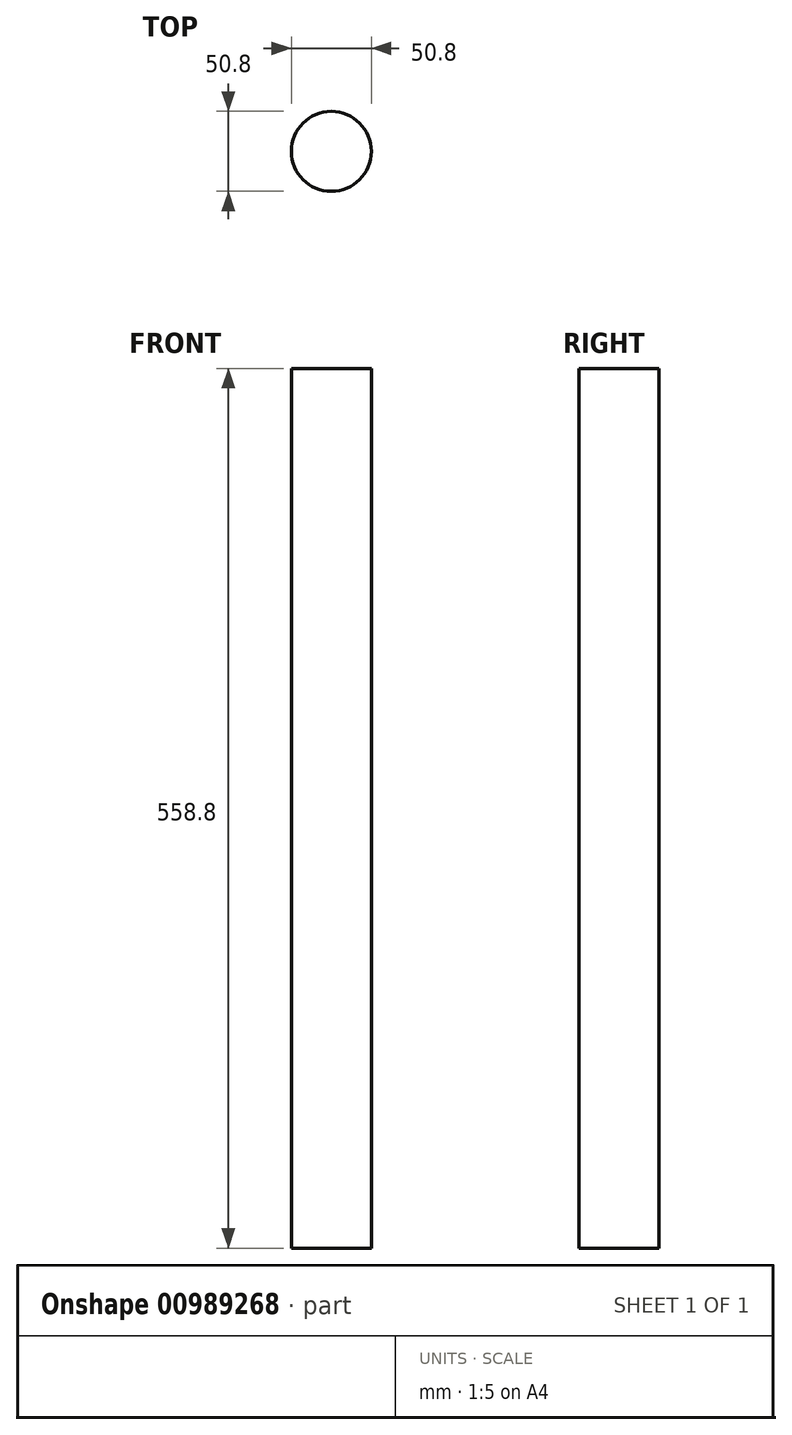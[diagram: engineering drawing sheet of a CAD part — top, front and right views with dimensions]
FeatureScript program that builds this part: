
annotation { "Feature Type Name" : "Feature", "Feature Type Description" : "" }
export const myFeature = defineFeature(function(context is Context, id is Id, definition is map)
    precondition{}
    {
        {
            var Q0;
            Q0=qCreatedBy(makeId("Top.planeOp"),FACE);
            var sketch = newSketch(context, id + "F0", { "sketchPlane" : qUnion([Q0])});
            skCircle(sketch, "E0", {"center": v(0, 0) * mm, "radius": 25.4 * mm});
            skSolve(sketch);
        }
        {
            var Q0;
            Q0 = qSketchRegion(id + "F0", true);
            extrude(context, id + "F1", {"entities" : qUnion([Q0]), "depth" : 558.8 * mm, "offsetDistance" : 25.4 * mm});
        }
    });
